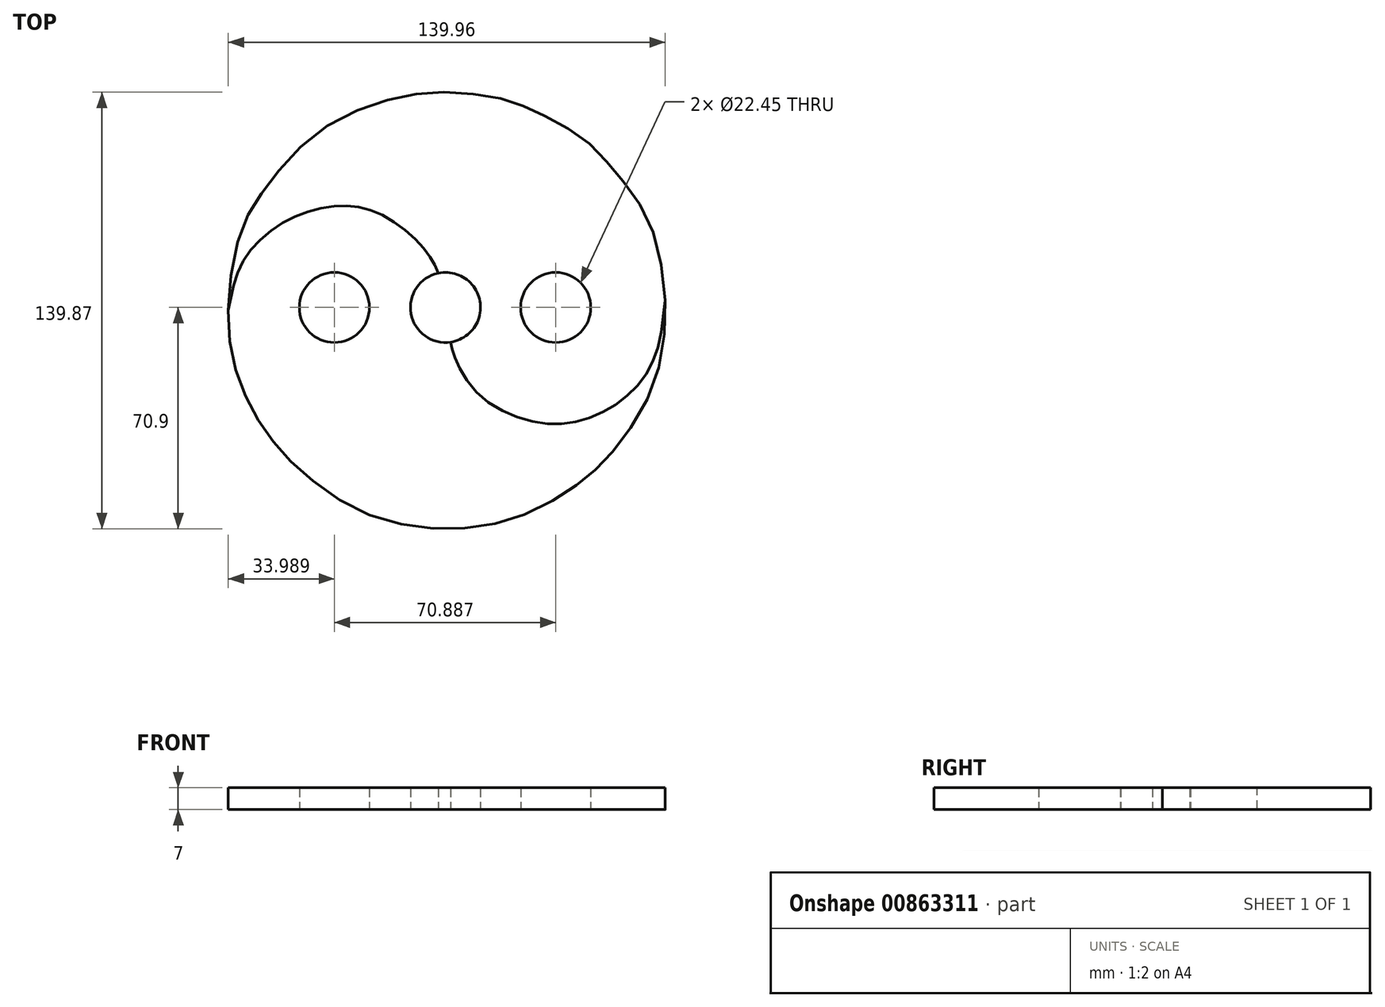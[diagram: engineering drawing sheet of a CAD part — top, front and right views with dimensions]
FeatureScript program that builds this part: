
annotation { "Feature Type Name" : "Feature", "Feature Type Description" : "" }
export const myFeature = defineFeature(function(context is Context, id is Id, definition is map)
    precondition{}
    {
        {
            var Q0;
            Q0=qCreatedBy(makeId("Top.planeOp"),FACE);
            var sketch = newSketch(context, id + "F0", { "sketchPlane" : qUnion([Q0])});
            skCircle(sketch, "E0", {"center": v(0, 0) * mm, "radius": 11.23 * mm});
            skCircle(sketch, "E1", {"center": v(-35.57, 0) * mm, "radius": 11.23 * mm});
            skCircle(sketch, "E2", {"center": v(35.32, 0) * mm, "radius": 11.23 * mm});
            skPoint(sketch, "E3.0.internal.snap0", {"position": v(0.38, 68.97) * mm});
            skFitSpline(sketch, "E3", {"points": [v(0, 68.97) * mm, v(18.55, 66.73) * mm, v(30.29, 62.18) * mm, v(44.18, 54.03) * mm, v(54.24, 43.74) * mm, v(64.77, 28.4) * mm, v(70.3, 2.3) * mm, v(66.45, -25.23) * mm, v(53.28, -46.55) * mm, v(42.5, -56.6) * mm, v(23.34, -67.14) * mm, v(0.38, -70.9) * mm, v(-25.03, -66.19) * mm, v(-46.59, -52.06) * mm, v(-58.08, -38.89) * mm, v(-66.46, -22.36) * mm, v(-69.55, -0.96) * mm, v(-65.27, 25.06) * mm, v(-57.12, 38.95) * mm, v(-41.08, 55.95) * mm, v(-18.33, 66.49) * mm, v(0, 68.97) * mm]});
            skFitSpline(sketch, "E4", {"points": [v(-69.55, -0.96) * mm, v(-64.79, 14.76) * mm, v(-51.62, 27.45) * mm, v(-34.61, 32.48) * mm, v(-20.24, 29.6) * mm, v(-6.83, 18.83) * mm, v(-2.27, 11) * mm], "startDerivative": vector(17.7, 94.73) * mm, "endDerivative": vector(26.9, -60.3) * mm});
            skFitSpline(sketch, "E5", {"points": [v(70.3, 2.3) * mm, v(66.93, -16.13) * mm, v(57.59, -28.83) * mm, v(43.22, -36.25) * mm, v(27.65, -36.5) * mm, v(10.41, -27.63) * mm, v(2.99, -15.9) * mm, v(1.72, -11.1) * mm], "startDerivative": vector(-11.4, -119.53) * mm, "endDerivative": vector(-10.04, 52.66) * mm});
            skSolve(sketch);
        }
        {
            var Q0;
            Q0=makeQuery(id+"F0.imprint","IMPRINT",FACE,{"disambiguationData":[TD([[makeQuery(id+"F0.imprint","IMPRINT",EDGE,{"derivedFrom":sQuery(id+"F0.wireOp",EDGE,"E2")}),-1.0]])]});
            extrude(context, id + "F1", {"entities" : qUnion([Q0]), "depth" : 7 * mm, "offsetDistance" : 25 * mm});
        }
        {
            var Q0;
            Q0=makeQuery(id+"F0.imprint","IMPRINT",FACE,{"disambiguationData":[TD([[makeQuery(id+"F0.imprint","IMPRINT",EDGE,{"derivedFrom":sQuery(id+"F0.wireOp",EDGE,"E1")}),-1.0]])]});
            extrude(context, id + "F2", {"entities" : qUnion([Q0]), "depth" : 7 * mm, "offsetDistance" : 25 * mm});
        }
    });
